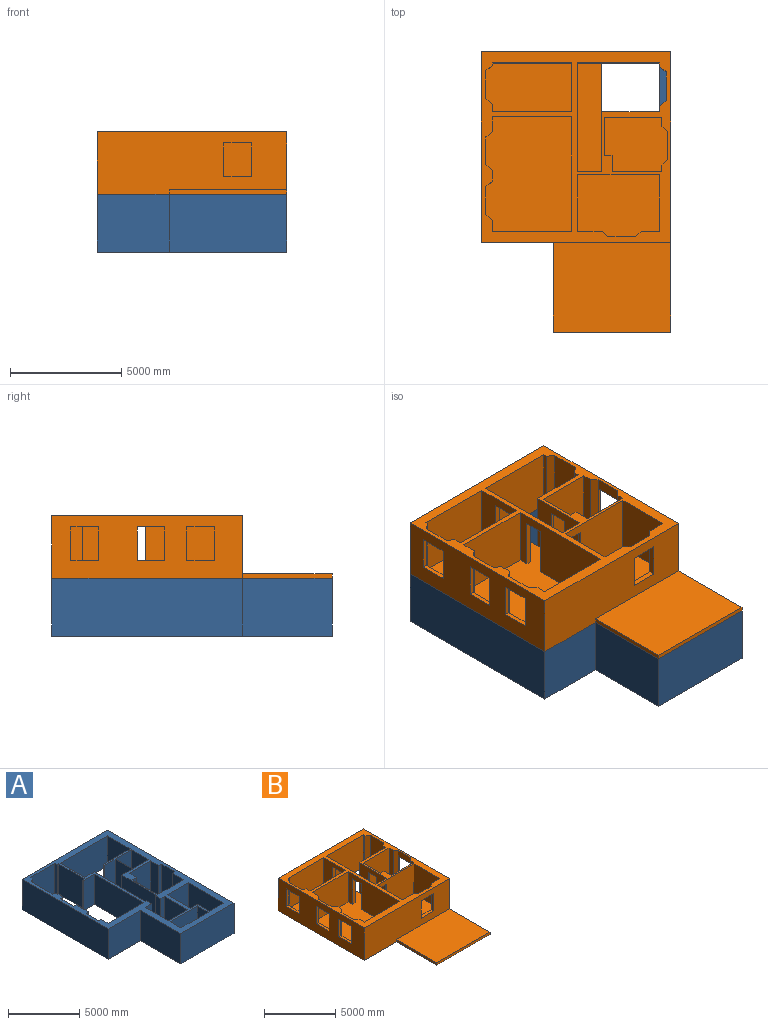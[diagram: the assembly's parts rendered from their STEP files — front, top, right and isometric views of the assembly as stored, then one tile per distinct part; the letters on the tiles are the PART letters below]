
ASSEMBLY  parts=2 mates=1
PART A: 80 faces, bbox 8490x12570x2600 mm
  f0: plane 8550x2600mm, normal (-1,0,0), area 22230000mm2, adj f1,f77,f78,f79
  f1: plane 3220x2600mm, normal (0,-1,0), area 8372000mm2, adj f0,f2,f78,f79
  f2: plane 4020x2600mm, normal (-1,0,0), area 10452000mm2, adj f1,f3,f78,f79
  f3: plane 5270x2600mm, normal (0,-1,0), area 13702000mm2, adj f2,f4,f78,f79
  f4: plane 12570x2600mm, normal (1,0,0), area 32682000mm2, adj f3,f77,f78,f79
  f5: plane 2600x1080mm, normal (1,0,0), area 2808000mm2, adj f6,f71,f78,f79
  f6: plane 2700x2600mm, normal (0,-1,0), area 7020000mm2, adj f5,f7,f78,f79
  f7: plane 2600x1080mm, normal (-1,0,0), area 2808000mm2, adj f6,f71,f78,f79
  f8: plane 2600x700mm, normal (0,1,0), area 1820000mm2, adj f9,f72,f78,f79
  f9: plane 2600x2300mm, normal (1,0,0), area 5980000mm2, adj f8,f10,f78,f79
  f10: plane 2600x2100mm, normal (0,-1,0), area 5460000mm2, adj f9,f11,f78,f79
  f11: plane 3520x2600mm, normal (-1,0,0), area 9152000mm2, adj f10,f12,f78,f79
  f12: plane 2600x1400mm, normal (0,1,0), area 3640000mm2, adj f11,f72,f78,f79
  f13: plane 2600x250mm, normal (0.2,0.98,0), area 662872.5mm2, adj f14,f73,f78,f79
  f14: plane 2600x1250mm, normal (1,0,0), area 3250000mm2, adj f13,f15,f78,f79
  f15: plane 2600x250mm, normal (0.2,-0.98,0), area 662872.5mm2, adj f14,f16,f78,f79
  f16: plane 2600x1160mm, normal (1,0,0), area 3016000mm2, adj f15,f17,f78,f79
  f17: plane 2600x250mm, normal (0.2,0.98,0), area 662872.5mm2, adj f16,f18,f78,f79
  f18: plane 2600x1250mm, normal (1,0,0), area 3250000mm2, adj f17,f19,f78,f79
  f19: plane 2600x250mm, normal (0.2,-0.98,0), area 662872.5mm2, adj f18,f20,f78,f79
  f20: plane 2600x380mm, normal (1,0,0), area 988000mm2, adj f19,f21,f78,f79
  f21: plane 2600x100mm, normal (0,-1,0), area 260000mm2, adj f20,f22,f78,f79
  f22: plane 2600x130mm, normal (1,0,0), area 338000mm2, adj f21,f23,f78,f79
  f23: plane 2600x100mm, normal (0,1,0), area 260000mm2, adj f22,f24,f78,f79
  f24: plane 2600x150mm, normal (1,0,0), area 390000mm2, adj f23,f25,f78,f79
  f25: plane 2600x250mm, normal (0.37,0.93,0), area 700071.4mm2, adj f24,f26,f78,f79
  f26: plane 2600x2150mm, normal (1,0,0), area 5590000mm2, adj f25,f27,f78,f79
  f27: plane 2600x250mm, normal (0.37,-0.93,0), area 700071.4mm2, adj f26,f28,f78,f79
  f28: plane 2600x50mm, normal (1,0,0), area 130000mm2, adj f27,f29,f78,f79
  f29: plane 2600x50mm, normal (0,-1,0), area 130000mm2, adj f28,f30,f78,f79
  f30: plane 2600x250mm, normal (0.96,-0.29,0), area 678619.9mm2, adj f29,f31,f78,f79
  f31: plane 2600x2350mm, normal (0,-1,0), area 6110000mm2, adj f30,f32,f78,f79
  f32: plane 2600x250mm, normal (-0.96,-0.29,0), area 678619.9mm2, adj f31,f33,f78,f79
  f33: plane 2600x100mm, normal (0,-1,0), area 260000mm2, adj f32,f34,f78,f79
  f34: plane 2600x2550mm, normal (-1,0,0), area 6630000mm2, adj f33,f35,f78,f79
  f35: plane 2600x220mm, normal (0,1,0), area 572000mm2, adj f34,f36,f78,f79
  f36: plane 2600x100mm, normal (-1,0,0), area 260000mm2, adj f35,f37,f78,f79
  f37: plane 2600x1120mm, normal (0,-1,0), area 2912000mm2, adj f36,f38,f78,f79
  f38: plane 4900x2600mm, normal (-1,0,0), area 12740000mm2, adj f37,f39,f78,f79
  f39: plane 3550x2600mm, normal (0,1,0), area 9230000mm2, adj f38,f73,f78,f79
  f40: plane 2600x2530mm, normal (1,0,0), area 6578000mm2, adj f41,f74,f78,f79
  f41: plane 2600x420mm, normal (0,-1,0), area 1092000mm2, adj f40,f42,f78,f79
  f42: plane 2600x720mm, normal (1,0,0), area 1872000mm2, adj f41,f43,f78,f79
  f43: plane 2600x2130mm, normal (0,-1,0), area 5538000mm2, adj f42,f44,f78,f79
  f44: plane 2600x800mm, normal (-1,0,0), area 2080000mm2, adj f43,f45,f78,f79
  f45: plane 2600x250mm, normal (-0.2,-0.98,0), area 662872.5mm2, adj f44,f46,f78,f79
  f46: plane 2600x1250mm, normal (-1,0,0), area 3250000mm2, adj f45,f47,f78,f79
  f47: plane 2600x250mm, normal (-0.2,0.98,0), area 662872.5mm2, adj f46,f48,f78,f79
  f48: plane 2600x1100mm, normal (-1,0,0), area 2860000mm2, adj f47,f74,f78,f79
  f49: plane 2600x90mm, normal (0,1,0), area 234000mm2, adj f50,f75,f78,f79
  f50: plane 2600x500mm, normal (-1,0,0), area 1300000mm2, adj f49,f51,f78,f79
  f51: plane 2600x380mm, normal (0,-1,0), area 988000mm2, adj f50,f52,f78,f79
  f52: plane 2600x2300mm, normal (-1,0,0), area 5980000mm2, adj f51,f53,f78,f79
  f53: plane 2600x1900mm, normal (0,1,0), area 4940000mm2, adj f52,f54,f78,f79
  f54: plane 2600x2300mm, normal (1,0,0), area 5980000mm2, adj f53,f55,f78,f79
  f55: plane 2600x640mm, normal (0,-1,0), area 1664000mm2, adj f54,f56,f78,f79
  f56: plane 2600x500mm, normal (1,0,0), area 1300000mm2, adj f55,f57,f78,f79
  f57: plane 2600x130mm, normal (0,1,0), area 338000mm2, adj f56,f58,f78,f79
  f58: plane 5110x2600mm, normal (1,0,0), area 13286000mm2, adj f57,f59,f78,f79
  f59: plane 2600x940mm, normal (0,1,0), area 2444000mm2, adj f58,f60,f78,f79
  f60: plane 2600x2440mm, normal (1,0,0), area 6344000mm2, adj f59,f61,f78,f79
  f61: plane 4700x2600mm, normal (0,-1,0), area 12220000mm2, adj f60,f62,f78,f79
  f62: plane 2600x2250mm, normal (-1,0,0), area 5850000mm2, adj f61,f63,f78,f79
  f63: plane 2660x2600mm, normal (0,1,0), area 6916000mm2, adj f62,f64,f78,f79
  f64: plane 2600x140mm, normal (-1,0,0), area 364000mm2, adj f63,f65,f78,f79
  f65: plane 2600x1020mm, normal (0,-1,0), area 2652000mm2, adj f64,f66,f78,f79
  f66: plane 2600x1700mm, normal (-1,0,0), area 4420000mm2, adj f65,f67,f78,f79
  f67: plane 2600x1020mm, normal (0,1,0), area 2652000mm2, adj f66,f75,f78,f79
  f68: plane 2600x1700mm, normal (-1,0,0), area 4420000mm2, adj f69,f76,f78,f79
  f69: plane 2600x1600mm, normal (0,1,0), area 4160000mm2, adj f68,f70,f78,f79
  f70: plane 2600x1700mm, normal (1,0,0), area 4420000mm2, adj f69,f76,f78,f79
  f71: plane 2700x2600mm, normal (0,1,0), area 7020000mm2, adj f5,f7,f78,f79
  f72: plane 2600x1220mm, normal (1,0,0), area 3172000mm2, adj f8,f12,f78,f79
  f73: plane 2600x630mm, normal (1,0,0), area 1638000mm2, adj f13,f39,f78,f79
  f74: plane 2600x2550mm, normal (0,1,0), area 6630000mm2, adj f40,f48,f78,f79
  f75: plane 3460x2600mm, normal (-1,0,0), area 8996000mm2, adj f49,f67,f78,f79
  f76: plane 2600x1600mm, normal (0,-1,0), area 4160000mm2, adj f68,f70,f78,f79
  f77: plane 8490x2600mm, normal (0,1,0), area 22074000mm2, adj f0,f4,f78,f79
  f78: plane 12570x8490mm, normal (0,0,1), area 23961950mm2, adj f0,f1,f2,f3,f4,f5,f6,f7
  f79: plane 12570x8490mm, normal (0,0,-1), area 23961950mm2, adj f0,f1,f2,f3,f4,f5,f6,f7
PART B: 96 faces, bbox 8490x12570x2800 mm
  f0: plane 1250x600mm, normal (0,1,0), area 750000mm2, adj f9,f19,f20,f76
  f1: plane 1250x600mm, normal (-1,0,0), area 750000mm2, adj f9,f25,f26,f73
  f2: plane 1250x600mm, normal (1,0,0), area 750000mm2, adj f9,f33,f34,f82
  f3: plane 1250x600mm, normal (1,0,0), area 750000mm2, adj f9,f43,f44,f85
  f4: plane 1250x600mm, normal (1,0,0), area 750000mm2, adj f9,f31,f40,f79
  f5: plane 8550x8490mm, normal (0,0,1), area 17545500mm2, adj f6,f7,f8,f12,f15,f16,f17,f18
  f6: plane 8550x2800mm, normal (-1,0,0), area 18315000mm2, adj f5,f10,f12,f16,f77,f78,f79,f80
  f7: plane 2690x2600mm, normal (-1,0,0), area 5102000mm2, adj f5,f9,f47,f57,f62,f63,f64
  f8: plane 3670x2600mm, normal (0,-1,0), area 7650000mm2, adj f5,f9,f17,f22,f65,f66,f67
  f9: plane 8150x7800mm, normal (0,0,1), area 49508800mm2, adj f0,f1,f2,f3,f4,f7,f8,f17
  f10: plane 12570x8490mm, normal (0,0,-1), area 87589900mm2, adj f6,f12,f13,f14,f15,f16,f49,f50
  f11: plane 5270x4020mm, normal (0,0,1), area 21185400mm2, adj f12,f13,f14,f15
  f12: plane 8490x2800mm, normal (0,-1,0), area 20843000mm2, adj f5,f6,f10,f11,f13,f15,f74,f75
  f13: plane 4020x200mm, normal (-1,0,0), area 804000mm2, adj f10,f11,f12,f14
  f14: plane 5270x200mm, normal (0,-1,0), area 1054000mm2, adj f10,f11,f13,f15
  f15: plane 12570x2800mm, normal (1,0,0), area 22869000mm2, adj f5,f10,f11,f12,f14,f16,f71,f72
  f16: plane 8490x2800mm, normal (0,1,0), area 23772000mm2, adj f5,f6,f10,f15
  f17: plane 2600x2530mm, normal (-1,0,0), area 6578000mm2, adj f5,f8,f9,f18
  f18: plane 2600x820mm, normal (0,1,0), area 2132000mm2, adj f5,f9,f17,f19
  f19: plane 2600x250mm, normal (-0.71,0.71,0), area 919238.8mm2, adj f0,f5,f9,f18,f75,f92
  f20: plane 2600x250mm, normal (0.71,0.71,0), area 919238.8mm2, adj f0,f5,f9,f21,f74,f92
  f21: plane 2600x1100mm, normal (0,1,0), area 2860000mm2, adj f5,f9,f20,f22
  f22: plane 2600x2530mm, normal (1,0,0), area 6578000mm2, adj f5,f8,f9,f21
  f23: plane 2600x2570mm, normal (0,-1,0), area 6682000mm2, adj f5,f9,f24,f55
  f24: plane 2600x400mm, normal (-1,0,0), area 1040000mm2, adj f5,f9,f23,f25
  f25: plane 2600x250mm, normal (-0.71,-0.71,0), area 919238.8mm2, adj f1,f5,f9,f24,f72,f94
  f26: plane 2600x250mm, normal (-0.71,0.71,0), area 919238.8mm2, adj f1,f5,f9,f27,f71,f94
  f27: plane 2600x310mm, normal (-1,0,0), area 806000mm2, adj f5,f9,f26,f28
  f28: plane 2600x2240mm, normal (0,1,0), area 5824000mm2, adj f5,f9,f27,f29
  f29: plane 2600x720mm, normal (1,0,0), area 1872000mm2, adj f5,f9,f28,f30
  f30: plane 2600x330mm, normal (0,1,0), area 858000mm2, adj f5,f9,f29,f55
  f31: plane 2600x300mm, normal (0.64,-0.77,0), area 1015332.5mm2, adj f4,f5,f9,f32,f77,f90
  f32: plane 2600x480mm, normal (1,0,0), area 1248000mm2, adj f5,f9,f31,f33
  f33: plane 2600x300mm, normal (0.64,0.77,0), area 1015332.5mm2, adj f2,f5,f9,f32,f81,f88
  f34: plane 2600x300mm, normal (0.64,-0.77,0), area 1015332.5mm2, adj f2,f5,f9,f35,f80,f88
  f35: plane 2600x650mm, normal (1,0,0), area 1690000mm2, adj f5,f9,f34,f36
  f36: plane 3560x2600mm, normal (0,-1,0), area 9256000mm2, adj f5,f9,f35,f37
  f37: plane 5130x2600mm, normal (-1,0,0), area 11424000mm2, adj f5,f9,f36,f38,f68,f69,f70
  f38: plane 3560x2600mm, normal (0,1,0), area 9256000mm2, adj f5,f9,f37,f39
  f39: plane 2600x500mm, normal (1,0,0), area 1300000mm2, adj f5,f9,f38,f40
  f40: plane 2600x300mm, normal (0.64,0.77,0), area 1015332.5mm2, adj f4,f5,f9,f39,f78,f90
  f41: plane 3560x2600mm, normal (0,1,0), area 9256000mm2, adj f5,f9,f42,f56
  f42: plane 2600x340mm, normal (1,0,0), area 884000mm2, adj f5,f9,f41,f43
  f43: plane 2600x300mm, normal (0.64,0.77,0), area 1015332.5mm2, adj f3,f5,f9,f42,f83,f86
  f44: plane 2600x300mm, normal (0.64,-0.77,0), area 1015332.5mm2, adj f3,f5,f9,f45,f84,f86
  f45: plane 2600x100mm, normal (1,0,0), area 260000mm2, adj f5,f9,f44,f46
  f46: plane 3560x2600mm, normal (0,-1,0), area 9256000mm2, adj f5,f9,f45,f56
  f47: plane 2600x1090mm, normal (0,1,0), area 942000mm2, adj f5,f7,f9,f48,f65,f66,f67
  f48: plane 4890x2600mm, normal (1,0,0), area 8886000mm2, adj f5,f9,f47,f49,f59,f60,f61,f68
  f49: plane 3690x2800mm, normal (0,-1,0), area 10114000mm2, adj f5,f9,f10,f48,f50,f58
  f50: plane 2800x150mm, normal (-1,0,0), area 420000mm2, adj f5,f10,f49,f51
  f51: plane 2800x300mm, normal (-0.64,-0.77,0), area 1093435mm2, adj f5,f10,f50,f52
  f52: plane 2800x1300mm, normal (-1,0,0), area 3640000mm2, adj f5,f10,f51,f53
  f53: plane 2800x300mm, normal (-0.64,0.77,0), area 1093435mm2, adj f5,f10,f52,f54
  f54: plane 2800x250mm, normal (-1,0,0), area 700000mm2, adj f5,f10,f53,f57
  f55: plane 2600x1740mm, normal (1,0,0), area 2632000mm2, adj f5,f9,f23,f30,f62,f63,f64
  f56: plane 2600x2190mm, normal (-1,0,0), area 3780000mm2, adj f5,f9,f41,f46,f59,f60,f61
  f57: plane 2800x2600mm, normal (0,1,0), area 7280000mm2, adj f5,f7,f10,f54,f58
  f58: plane 2200x200mm, normal (1,0,0), area 440000mm2, adj f9,f10,f49,f57
  f59: plane 2200x240mm, normal (0,-1,0), area 528000mm2, adj f9,f48,f56,f61
  f60: plane 2200x240mm, normal (0,1,0), area 528000mm2, adj f9,f48,f56,f61
  f61: plane 870x240mm, normal (0,0,-1), area 208800mm2, adj f48,f56,f59,f60
  f62: plane 2200x140mm, normal (0,-1,0), area 308000mm2, adj f7,f9,f55,f64
  f63: plane 2200x140mm, normal (0,1,0), area 308000mm2, adj f7,f9,f55,f64
  f64: plane 860x140mm, normal (0,0,-1), area 120400mm2, adj f7,f55,f62,f63
  f65: plane 2200x130mm, normal (1,0,0), area 286000mm2, adj f8,f9,f47,f67
  f66: plane 2200x130mm, normal (-1,0,0), area 286000mm2, adj f8,f9,f47,f67
  f67: plane 860x130mm, normal (0,0,-1), area 111800mm2, adj f8,f47,f65,f66
  f68: plane 2200x240mm, normal (0,-1,0), area 528000mm2, adj f9,f37,f48,f70
  f69: plane 2200x240mm, normal (0,1,0), area 528000mm2, adj f9,f37,f48,f70
  f70: plane 870x240mm, normal (0,0,-1), area 208800mm2, adj f37,f48,f68,f69
  f71: plane 1500x140mm, normal (0,1,0), area 210000mm2, adj f15,f26,f73,f95
  f72: plane 1500x140mm, normal (0,-1,0), area 210000mm2, adj f15,f25,f73,f95
  f73: plane 1250x140mm, normal (0,0,1), area 175000mm2, adj f1,f15,f71,f72
  f74: plane 1500x250mm, normal (1,0,0), area 375000mm2, adj f12,f20,f76,f93
  f75: plane 1500x250mm, normal (-1,0,0), area 375000mm2, adj f12,f19,f76,f93
  f76: plane 1250x250mm, normal (0,0,1), area 312500mm2, adj f0,f12,f74,f75
  f77: plane 1500x200mm, normal (0,-1,0), area 300000mm2, adj f6,f31,f79,f91
  f78: plane 1500x200mm, normal (0,1,0), area 300000mm2, adj f6,f40,f79,f91
  f79: plane 1250x200mm, normal (0,0,1), area 250000mm2, adj f4,f6,f77,f78
  f80: plane 1500x200mm, normal (0,-1,0), area 300000mm2, adj f6,f34,f82,f89
  f81: plane 1500x200mm, normal (0,1,0), area 300000mm2, adj f6,f33,f82,f89
  f82: plane 1250x200mm, normal (0,0,1), area 250000mm2, adj f2,f6,f80,f81
  f83: plane 1500x200mm, normal (0,1,0), area 300000mm2, adj f6,f43,f85,f87
  f84: plane 1500x200mm, normal (0,-1,0), area 300000mm2, adj f6,f44,f85,f87
  f85: plane 1250x200mm, normal (0,0,1), area 250000mm2, adj f3,f6,f83,f84
  f86: plane 1250x500mm, normal (1,0,0), area 625000mm2, adj f5,f43,f44,f87
  f87: plane 1250x200mm, normal (0,0,-1), area 250000mm2, adj f6,f83,f84,f86
  f88: plane 1250x500mm, normal (1,0,0), area 625000mm2, adj f5,f33,f34,f89
  f89: plane 1250x200mm, normal (0,0,-1), area 250000mm2, adj f6,f80,f81,f88
  f90: plane 1250x500mm, normal (1,0,0), area 625000mm2, adj f5,f31,f40,f91
  f91: plane 1250x200mm, normal (0,0,-1), area 250000mm2, adj f6,f77,f78,f90
  f92: plane 1250x500mm, normal (0,1,0), area 625000mm2, adj f5,f19,f20,f93
  f93: plane 1250x250mm, normal (0,0,-1), area 312500mm2, adj f12,f74,f75,f92
  f94: plane 1250x500mm, normal (-1,0,0), area 625000mm2, adj f5,f25,f26,f95
  f95: plane 1250x140mm, normal (0,0,-1), area 175000mm2, adj f15,f71,f72,f94
PLACE A t=(500,500,200)mm
PLACE B t=(600,600,2800)mm
MATE fastened B.f10 <-> A.f78  axis (0,0,-1) through (0,0,2800)mm
